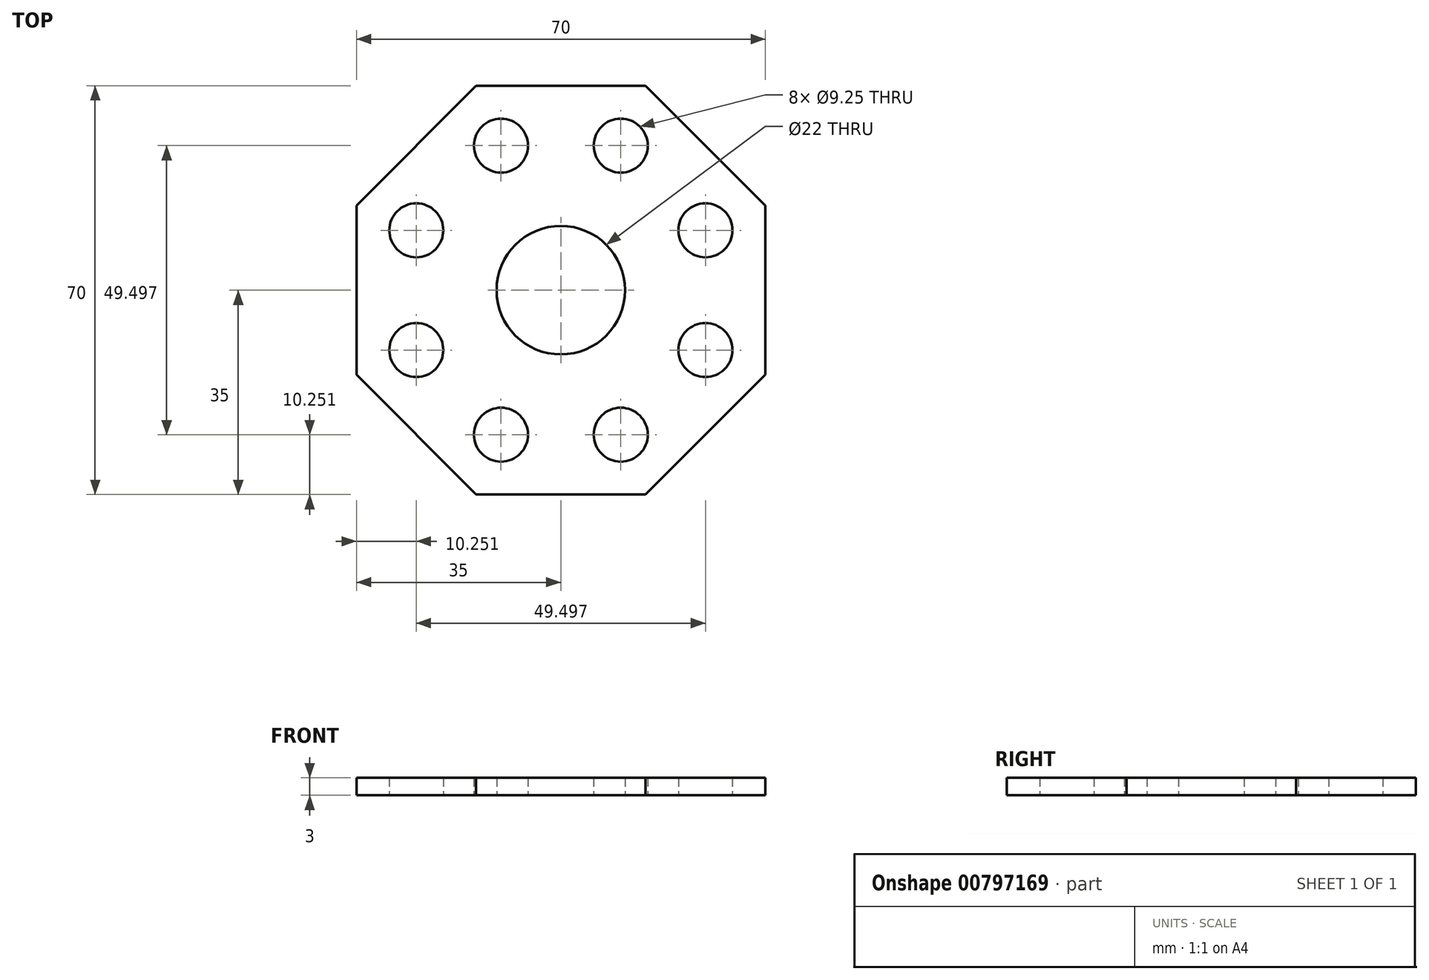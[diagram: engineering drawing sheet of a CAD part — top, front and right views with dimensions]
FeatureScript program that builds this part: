
annotation { "Feature Type Name" : "Feature", "Feature Type Description" : "" }
export const myFeature = defineFeature(function(context is Context, id is Id, definition is map)
    precondition{}
    {
        {
            var Q0;
            Q0=qCreatedBy(makeId("Top.planeOp"),FACE);
            var sketch = newSketch(context, id + "F0", { "sketchPlane" : qUnion([Q0])});
            skArc(sketch, "E0", {"start": v(11, 0) * mm, "mid": v(7.78, 7.78) * mm, "end": v(0, 11) * mm});
            skLineSegment(sketch, "E1.5", {"start": v(14.5, 35) * mm, "end": v(35, 14.5) * mm});
            skCircle(sketch, "E2", {"center": v(10.25, 24.75) * mm, "radius": 4.62 * mm});
            skCircle(sketch, "E3", {"center": v(24.75, 10.25) * mm, "radius": 4.62 * mm});
            skLineSegment(sketch, "E4.1.1", {"start": v(-35, 14.5) * mm, "end": v(-14.5, 35) * mm});
            skCircle(sketch, "E4.1.5", {"center": v(-24.75, 10.25) * mm, "radius": 4.62 * mm});
            skCircle(sketch, "E4.1.6", {"center": v(-10.25, 24.75) * mm, "radius": 4.62 * mm});
            skArc(sketch, "E4.1.7", {"start": v(0, 11) * mm, "mid": v(-7.78, 7.78) * mm, "end": v(-11, 0) * mm});
            skLineSegment(sketch, "E4.2.0", {"start": v(0, -35) * mm, "end": v(-14.5, -35) * mm});
            skLineSegment(sketch, "E4.2.1", {"start": v(-14.5, -35) * mm, "end": v(-35, -14.5) * mm});
            skCircle(sketch, "E4.2.5", {"center": v(-10.25, -24.75) * mm, "radius": 4.62 * mm});
            skCircle(sketch, "E4.2.6", {"center": v(-24.75, -10.25) * mm, "radius": 4.62 * mm});
            skArc(sketch, "E4.2.7", {"start": v(-11, 0) * mm, "mid": v(-7.78, -7.78) * mm, "end": v(0, -11) * mm});
            skLineSegment(sketch, "E4.3.1", {"start": v(35, -14.5) * mm, "end": v(14.5, -35) * mm});
            skLineSegment(sketch, "E4.3.2", {"start": v(14.5, -35) * mm, "end": v(0, -35) * mm});
            skCircle(sketch, "E4.3.5", {"center": v(24.75, -10.25) * mm, "radius": 4.62 * mm});
            skCircle(sketch, "E4.3.6", {"center": v(10.25, -24.75) * mm, "radius": 4.62 * mm});
            skArc(sketch, "E4.3.7", {"start": v(0, -11) * mm, "mid": v(7.78, -7.78) * mm, "end": v(11, 0) * mm});
            skLineSegment(sketch, "E5", {"start": v(-35, 14.5) * mm, "end": v(-35, -14.5) * mm});
            skLineSegment(sketch, "E6", {"start": v(35, 14.5) * mm, "end": v(35, -14.5) * mm});
            skLineSegment(sketch, "E7", {"start": v(-14.5, 35) * mm, "end": v(14.5, 35) * mm});
            skSolve(sketch);
        }
        {
            var Q0;
            Q0 = qSketchRegion(id + "F0", true);
            extrude(context, id + "F1", {"entities" : qUnion([Q0]), "depth" : 3 * mm, "offsetDistance" : 25 * mm});
        }
    });
